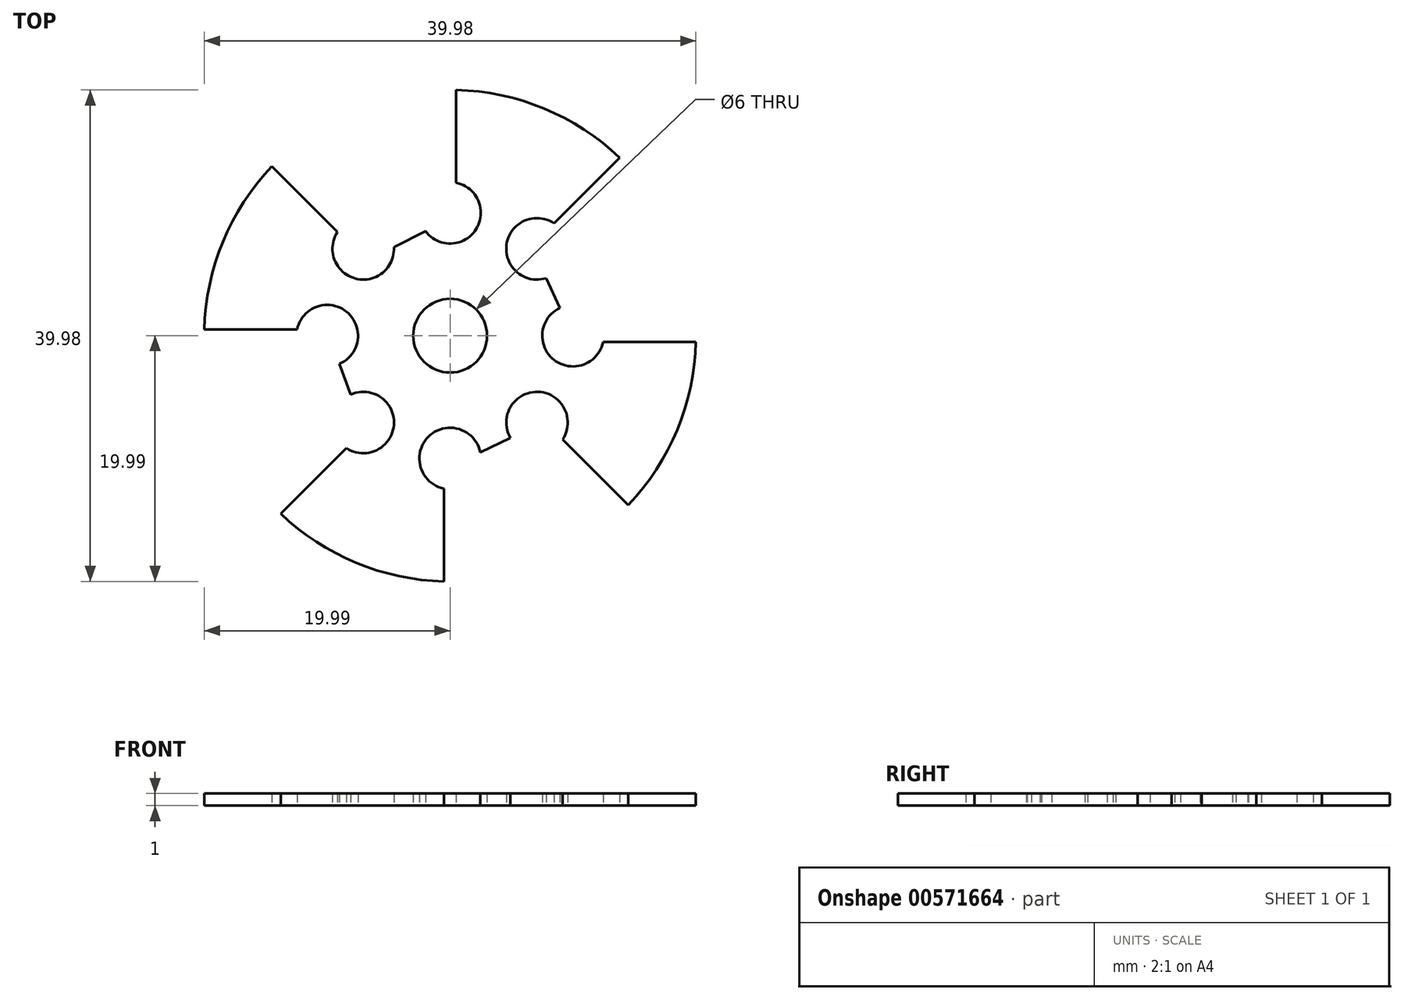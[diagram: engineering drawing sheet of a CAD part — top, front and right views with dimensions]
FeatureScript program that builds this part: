
annotation { "Feature Type Name" : "Feature", "Feature Type Description" : "" }
export const myFeature = defineFeature(function(context is Context, id is Id, definition is map)
    precondition{}
    {
        {
            var Q0;
            Q0=qCreatedBy(makeId("Top.planeOp"),FACE);
            var sketch = newSketch(context, id + "F0", { "sketchPlane" : qUnion([Q0])});
            skCircle(sketch, "E0", {"center": v(0, 0) * mm, "radius": 20 * mm});
            skCircle(sketch, "E1", {"center": v(0, 0) * mm, "radius": 3 * mm});
            skLineSegment(sketch, "E2.bottom", {"start": v(-0.5, 20) * mm, "end": v(0.5, 20) * mm});
            skLineSegment(sketch, "E2.left", {"start": v(-0.5, 20) * mm, "end": v(-0.5, 12.44) * mm});
            skLineSegment(sketch, "E2.right", {"start": v(0.5, 20) * mm, "end": v(0.5, 12.44) * mm});
            skArc(sketch, "E3", {"start": v(-0.5, 12.44) * mm, "mid": v(0, 7.5) * mm, "end": v(0.5, 12.44) * mm});
            skLineSegment(sketch, "E4.1.0", {"start": v(-14.5, 13.78) * mm, "end": v(-13.78, 14.5) * mm});
            skLineSegment(sketch, "E4.1.1", {"start": v(-13.78, 14.5) * mm, "end": v(-8.45, 9.15) * mm});
            skArc(sketch, "E4.1.2", {"start": v(-9.15, 8.45) * mm, "mid": v(-5.3, 5.3) * mm, "end": v(-8.45, 9.15) * mm});
            skLineSegment(sketch, "E4.1.3", {"start": v(-14.5, 13.78) * mm, "end": v(-9.15, 8.45) * mm});
            skLineSegment(sketch, "E4.2.0", {"start": v(-20, -0.5) * mm, "end": v(-20, 0.5) * mm});
            skLineSegment(sketch, "E4.2.1", {"start": v(-20, 0.5) * mm, "end": v(-12.44, 0.5) * mm});
            skArc(sketch, "E4.2.2", {"start": v(-12.44, -0.5) * mm, "mid": v(-7.5, 0) * mm, "end": v(-12.44, 0.5) * mm});
            skLineSegment(sketch, "E4.2.3", {"start": v(-20, -0.5) * mm, "end": v(-12.44, -0.5) * mm});
            skLineSegment(sketch, "E4.3.0", {"start": v(-13.78, -14.5) * mm, "end": v(-14.5, -13.78) * mm});
            skLineSegment(sketch, "E4.3.1", {"start": v(-14.5, -13.78) * mm, "end": v(-9.15, -8.45) * mm});
            skArc(sketch, "E4.3.2", {"start": v(-8.45, -9.15) * mm, "mid": v(-5.3, -5.3) * mm, "end": v(-9.15, -8.45) * mm});
            skLineSegment(sketch, "E4.3.3", {"start": v(-13.78, -14.5) * mm, "end": v(-8.45, -9.15) * mm});
            skLineSegment(sketch, "E4.4.0", {"start": v(0.5, -20) * mm, "end": v(-0.5, -20) * mm});
            skLineSegment(sketch, "E4.4.1", {"start": v(-0.5, -20) * mm, "end": v(-0.5, -12.44) * mm});
            skArc(sketch, "E4.4.2", {"start": v(0.5, -12.44) * mm, "mid": v(0, -7.5) * mm, "end": v(-0.5, -12.44) * mm});
            skLineSegment(sketch, "E4.4.3", {"start": v(0.5, -20) * mm, "end": v(0.5, -12.44) * mm});
            skLineSegment(sketch, "E4.5.0", {"start": v(14.5, -13.78) * mm, "end": v(13.78, -14.5) * mm});
            skLineSegment(sketch, "E4.5.1", {"start": v(13.78, -14.5) * mm, "end": v(8.45, -9.15) * mm});
            skArc(sketch, "E4.5.2", {"start": v(9.15, -8.45) * mm, "mid": v(5.3, -5.3) * mm, "end": v(8.45, -9.15) * mm});
            skLineSegment(sketch, "E4.5.3", {"start": v(14.5, -13.78) * mm, "end": v(9.15, -8.45) * mm});
            skLineSegment(sketch, "E4.6.0", {"start": v(20, 0.5) * mm, "end": v(20, -0.5) * mm});
            skLineSegment(sketch, "E4.6.1", {"start": v(20, -0.5) * mm, "end": v(12.44, -0.5) * mm});
            skArc(sketch, "E4.6.2", {"start": v(12.44, 0.5) * mm, "mid": v(7.5, 0) * mm, "end": v(12.44, -0.5) * mm});
            skLineSegment(sketch, "E4.6.3", {"start": v(20, 0.5) * mm, "end": v(12.44, 0.5) * mm});
            skLineSegment(sketch, "E4.7.0", {"start": v(13.78, 14.5) * mm, "end": v(14.5, 13.78) * mm});
            skLineSegment(sketch, "E4.7.1", {"start": v(14.5, 13.78) * mm, "end": v(9.15, 8.45) * mm});
            skArc(sketch, "E4.7.2", {"start": v(8.45, 9.15) * mm, "mid": v(5.3, 5.3) * mm, "end": v(9.15, 8.45) * mm});
            skLineSegment(sketch, "E4.7.3", {"start": v(13.78, 14.5) * mm, "end": v(8.45, 9.15) * mm});
            skLineSegment(sketch, "E5", {"start": v(-4.57, 7.2) * mm, "end": v(-2, 8.5) * mm});
            skLineSegment(sketch, "E6", {"start": v(7.81, 4.68) * mm, "end": v(8.92, 2.26) * mm});
            skLineSegment(sketch, "E7", {"start": v(4.9, -8.31) * mm, "end": v(2.45, -9.49) * mm});
            skLineSegment(sketch, "E8", {"start": v(-8.08, -4.78) * mm, "end": v(-9, -2.3) * mm});
            skSolve(sketch);
        }
        {
            var Q0;
            Q0=makeQuery(id+"F0.imprint","IMPRINT",FACE,{"disambiguationData":[TD([[makeQuery(id+"F0.imprint","IMPRINT",EDGE,{"derivedFrom":sQuery(id+"F0.wireOp",EDGE,"E1")}),-1.0]])]});
            extrude(context, id + "F1", {"entities" : qUnion([Q0]), "depth" : 1 * mm, "offsetDistance" : 25.4 * mm});
        }
    });
